# Revit family: QF_Kelvinator_738343_KCHUCWT48R-220_2-Door_220V_Refrigerated_Work_Top_48Long
name_source: partatom
category: Specialty Equipment
units: mm (PartAtom-declared; Revit-internal decimal feet)

## family parameters
Always vertical = Yes
Cut with Voids When Loaded = No
Part Type = Normal
Room Calculation Point = No
Round Connector Dimension = Use Diameter
Shared = No
Work Plane-Based = No

## types (1)
- QF_Kelvinator_738343_KCHUCWT48R-220_2-Door_220V_Refrigerated_Work_Top_48Long
    Apparent Power = 0 VA
    Conn Conduit = Yes
    Cycle = 50 Hz
    Default Elevation = 0"
    Depth = 29 15/16"
    Description = 2-Door 220V Refrigerated Work Top 48" Long
    Elec Conn Connection Height = 0"
    Elec Conn RI Height = 0"
    FL Amps = 3 A
    Foodservice Equipment Identifier = Yes
    HP = 1/4
    Height = 39 5/8"
    Identify Quantity as Lot = Yes
    Item Number = 738343
    Length = 48 1/4"
    Manufacturer = Kelvinator Commercial
    Max Overcurrent Protection = 0 A
    Min Ckt Ampacity = 0 A
    Model = 738343 (KCHUCWT48R-220)
    Number of Poles = 1
    Phase = 1
    Refrigerant Type = R290
    Volts = 220 V
    Watts = 660 W
    Weight in Pounds = 280

## geometry (parser evidence)
native form markers: Sweep x6
no freeform markers — native parametric forms only
